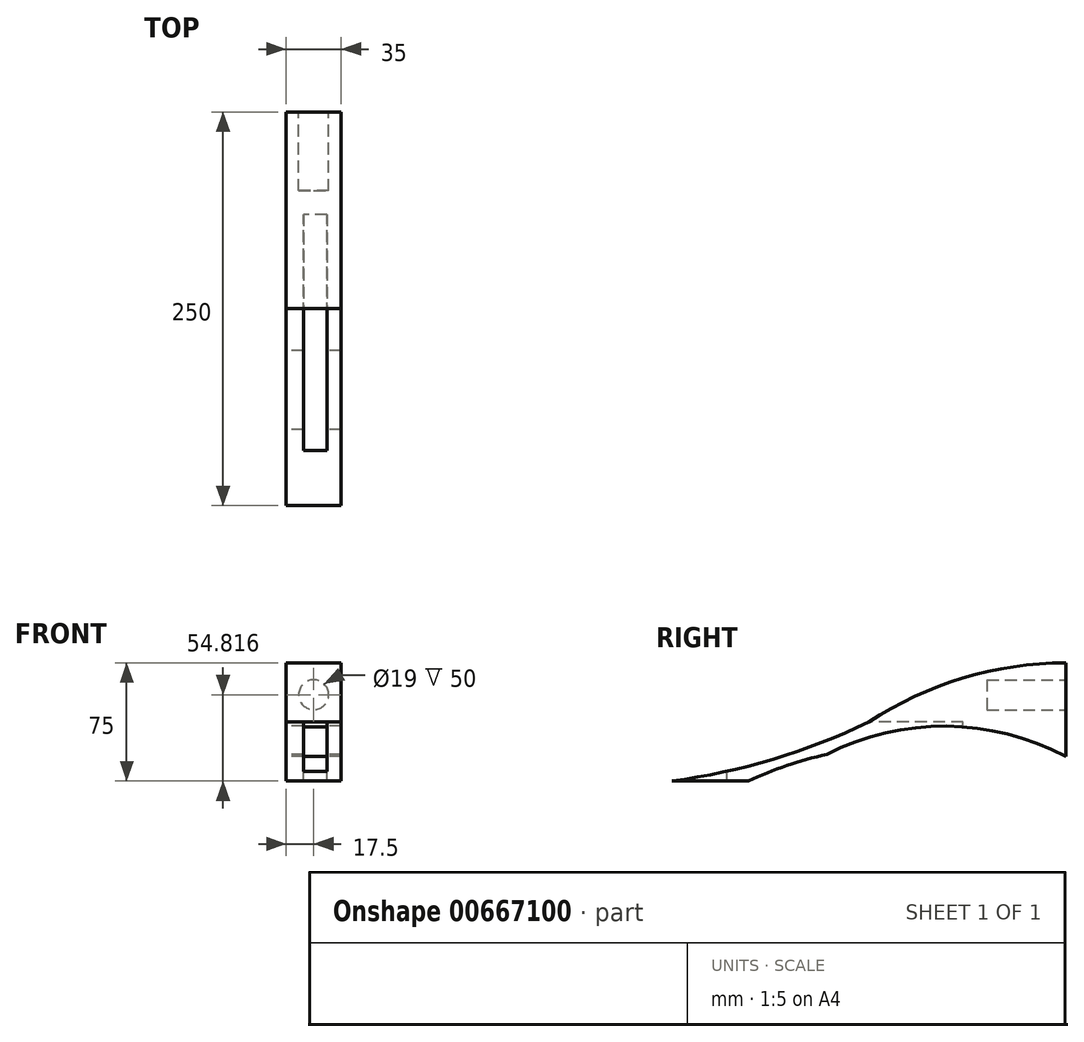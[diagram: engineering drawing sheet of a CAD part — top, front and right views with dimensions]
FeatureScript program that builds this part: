
annotation { "Feature Type Name" : "Feature", "Feature Type Description" : "" }
export const myFeature = defineFeature(function(context is Context, id is Id, definition is map)
    precondition{}
    {
        {
            var Q0;
            Q0=qCreatedBy(makeId("Right.planeOp"),FACE);
            var sketch = newSketch(context, id + "F0", { "sketchPlane" : qUnion([Q0])});
            skLineSegment(sketch, "E0.bottom", {"start": v(-125, 37.5) * mm, "end": v(125, 37.5) * mm});
            skLineSegment(sketch, "E0.top", {"start": v(-125, -37.5) * mm, "end": v(125, -37.5) * mm});
            skLineSegment(sketch, "E0.left", {"start": v(-125, 37.5) * mm, "end": v(-125, -37.5) * mm});
            skLineSegment(sketch, "E0.right", {"start": v(125, 37.5) * mm, "end": v(125, -37.5) * mm});
            skPoint(sketch, "E0.middle", {"position": v(0, 0) * mm});
            skSolve(sketch);
        }
        {
            var Q0;
            Q0=makeQuery(id+"F0.imprint","IMPRINT",FACE,{"disambiguationData":[TD([[makeQuery(id+"F0.imprint","IMPRINT",EDGE,{"derivedFrom":sQuery(id+"F0.wireOp",EDGE,"E0.bottom")}),-1.0]])]});
            extrude(context, id + "F1", {"entities" : qUnion([Q0]), "endBound" : BoundingType.SYMMETRIC, "depth" : 35 * mm, "offsetDistance" : 25 * mm});
        }
        {
            var Q0;
            Q0=makeQuery(id+"F1.opExtrude","CAP_FACE",FACE,{"disambiguationData":[OSD([sQuery(id+"F0.wireOp",EDGE,"E0.bottom"),sQuery(id+"F0.wireOp",EDGE,"E0.top"),sQuery(id+"F0.wireOp",EDGE,"E0.left"),sQuery(id+"F0.wireOp",EDGE,"E0.right")])],"isStart":true});
            var sketch = newSketch(context, id + "F2", { "sketchPlane" : qUnion([Q0])});
            skArc(sketch, "E1", {"start": v(0, 0) * mm, "mid": v(-59.75, 27.92) * mm, "end": v(-125, 37.5) * mm});
            skArc(sketch, "E2", {"start": v(0, 0) * mm, "mid": v(61.01, -23.71) * mm, "end": v(125, -37.5) * mm});
            skArc(sketch, "E3", {"start": v(76.61, -37.5) * mm, "mid": v(-24.2, -15.1) * mm, "end": v(-125, -37.5) * mm});
            skArc(sketch, "E4", {"start": v(26.68, -20.6) * mm, "mid": v(-49.33, -2.64) * mm, "end": v(-125, -21.95) * mm});
            skSolve(sketch);
        }
        {
            var Q0;
            Q0=makeQuery(id+"F2.imprint","IMPRINT",FACE,{"disambiguationData":[TD([[makeQuery(id+"F2.imprint","IMPRINT",EDGE,{"derivedFrom":sQuery(id+"F2.wireOp",EDGE,"E1")}),-1.0]])]});
            var Q1;
            {var subQ0=sQuery(id+"F2.wireOp",EDGE,"E3");Q1=makeQuery(id+"F2.imprint","IMPRINT",FACE,{"disambiguationData":[TD([[makeQuery(id+"F2.imprint","IMPRINT",EDGE,{"derivedFrom":subQ0}),1.0]])]});}
            var Q2;
            {var subQ3=sQuery(id+"F2.wireOp",EDGE,"E4");Q2=makeQuery(id+"F2.imprint","IMPRINT",FACE,{"disambiguationData":[TD([[makeQuery(id+"F2.imprint","IMPRINT",EDGE,{"derivedFrom":subQ3}),1.0]])]});}
            extrude(context, id + "F3", {"entities" : qUnion([Q0, Q1, Q2]), "operationType" : NewBodyOperationType.REMOVE, "endBound" : BoundingType.THROUGH_ALL, "oppositeDirection" : true, "depth" : 25 * mm, "offsetDistance" : 25 * mm});
        }
        {
            var Q0;
            Q0=makeQuery(id+"F1.opExtrude","SWEPT_FACE",FACE,{"disambiguationData":[OSD([sQuery(id+"F0.wireOp",EDGE,"E0.right")])]});
            var sketch = newSketch(context, id + "F4", { "sketchPlane" : qUnion([Q0])});
            skCircle(sketch, "E5", {"center": v(0, 17.32) * mm, "radius": 9.5 * mm});
            skSolve(sketch);
        }
        {
            var Q0;
            Q0=makeQuery(id+"F4.imprint","IMPRINT",FACE,{"disambiguationData":[TD([[makeQuery(id+"F4.imprint","IMPRINT",EDGE,{"derivedFrom":sQuery(id+"F4.wireOp",EDGE,"E5")}),1.0]])]});
            extrude(context, id + "F5", {"entities" : qUnion([Q0]), "operationType" : NewBodyOperationType.REMOVE, "oppositeDirection" : true, "depth" : 50 * mm, "offsetDistance" : 25 * mm});
        }
        {
            var Q0;
            Q0=qCreatedBy(makeId("Top.planeOp"),FACE);
            var sketch = newSketch(context, id + "F6", { "sketchPlane" : qUnion([Q0])});
            skLineSegment(sketch, "E6", {"start": v(-6.59, 59.9) * mm, "end": v(-6.59, -90.1) * mm});
            skLineSegment(sketch, "E7", {"start": v(-6.59, -90.1) * mm, "end": v(8.41, -90.1) * mm});
            skLineSegment(sketch, "E8", {"start": v(-6.59, 59.9) * mm, "end": v(8.41, 59.9) * mm});
            skLineSegment(sketch, "E9", {"start": v(8.41, 59.9) * mm, "end": v(8.41, -90.1) * mm});
            skSolve(sketch);
        }
        {
            var Q0;
            Q0 = qSketchRegion(id + "F6", true);
            extrude(context, id + "F7", {"entities" : qUnion([Q0]), "operationType" : NewBodyOperationType.REMOVE, "endBound" : BoundingType.THROUGH_ALL, "oppositeDirection" : true, "depth" : 25 * mm, "offsetDistance" : 25 * mm});
        }
    });
